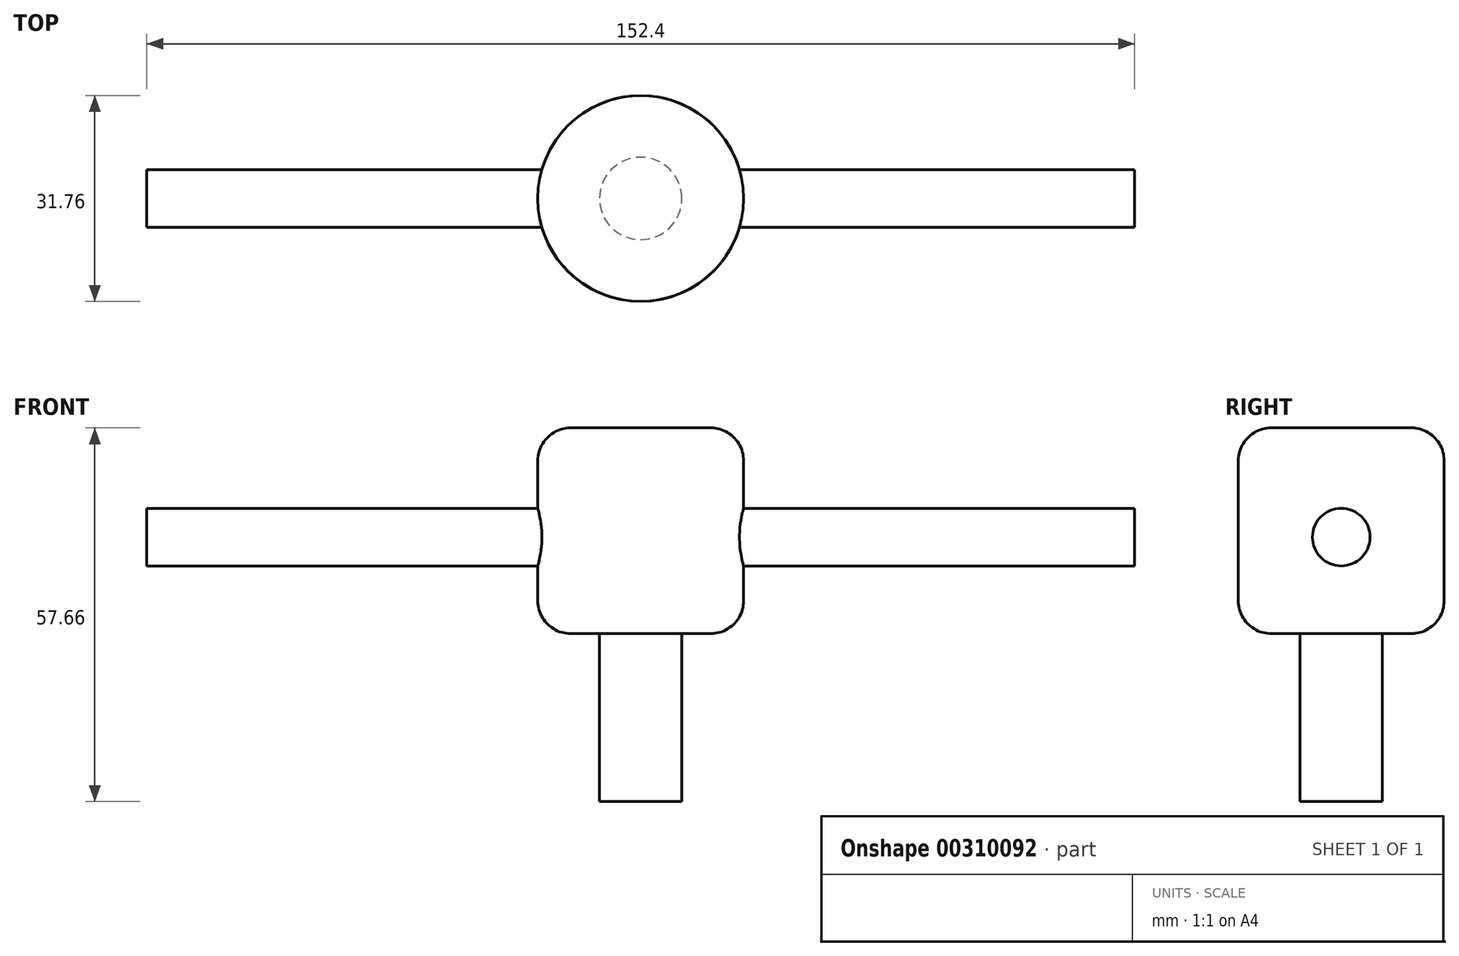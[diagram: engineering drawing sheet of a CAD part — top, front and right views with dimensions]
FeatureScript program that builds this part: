
annotation { "Feature Type Name" : "Feature", "Feature Type Description" : "" }
export const myFeature = defineFeature(function(context is Context, id is Id, definition is map)
    precondition{}
    {
        {
            var Q0;
            Q0=qCreatedBy(makeId("Top.planeOp"),FACE);
            var sketch = newSketch(context, id + "F0", { "sketchPlane" : qUnion([Q0])});
            skCircle(sketch, "E0", {"center": v(0, 0) * mm, "radius": 15.88 * mm});
            skSolve(sketch);
        }
        {
            var Q0;
            Q0 = qSketchRegion(id + "F0", true);
            extrude(context, id + "F1", {"entities" : qUnion([Q0]), "depth" : 31.75 * mm});
        }
        {
            var Q0;
            Q0=qCreatedBy(makeId("Right.planeOp"),FACE);
            var sketch = newSketch(context, id + "F2", { "sketchPlane" : qUnion([Q0])});
            skCircle(sketch, "E1", {"center": v(0, 14.9) * mm, "radius": 4.45 * mm});
            skSolve(sketch);
        }
        {
            var Q0;
            Q0 = qSketchRegion(id + "F2", true);
            extrude(context, id + "F3", {"entities" : qUnion([Q0]), "operationType" : NewBodyOperationType.ADD, "depth" : 76.2 * mm});
        }
        {
            var Q0;
            Q0=qCreatedBy(makeId("Right.planeOp"),FACE);
            var sketch = newSketch(context, id + "F4", { "sketchPlane" : qUnion([Q0])});
            skCircle(sketch, "E2", {"center": v(0, 14.9) * mm, "radius": 4.45 * mm});
            skSolve(sketch);
        }
        {
            var Q0;
            Q0 = qSketchRegion(id + "F4", true);
            extrude(context, id + "F5", {"entities" : qUnion([Q0]), "operationType" : NewBodyOperationType.ADD, "oppositeDirection" : true, "depth" : 76.2 * mm});
        }
        {
            var Q0;
            Q0=makeQuery(id+"F1.opExtrude","CAP_FACE",FACE,{"disambiguationData":[OSD([sQuery(id+"F0.wireOp",EDGE,"E0")])],"isStart":true});
            var sketch = newSketch(context, id + "F6", { "sketchPlane" : qUnion([Q0])});
            skCircle(sketch, "E3", {"center": v(0, 0) * mm, "radius": 6.35 * mm});
            skSolve(sketch);
        }
        {
            var Q0;
            Q0 = qSketchRegion(id + "F6", true);
            extrude(context, id + "F7", {"entities" : qUnion([Q0]), "operationType" : NewBodyOperationType.ADD, "depth" : 25.9 * mm});
        }
        {
            var Q0;
            Q0=makeQuery(id+"F1.opExtrude","CAP_EDGE",EDGE,{"disambiguationData":[OSD([sQuery(id+"F0.wireOp",EDGE,"E0")])],"isStart":false});
            var Q1;
            Q1=makeQuery(id+"F1.opExtrude","CAP_EDGE",EDGE,{"disambiguationData":[OSD([sQuery(id+"F0.wireOp",EDGE,"E0")])],"isStart":true});
            fillet(context, id + "F8", {"entities" : qUnion([Q0, Q1]), "radius" : 5.08 * mm, "tangentPropagation" : true, "allowEdgeOverflow" : false});
        }
    });
